# Revit family: КСФ К2 ЕС_Eng
name_source: partatom
category: Mechanical Equipment
units: mm (PartAtom-declared; Revit-internal decimal feet)

## family parameters
Always vertical = Yes
Classification = None
Cut with Voids When Loaded = No
Part Type = Normal
Room Calculation Point = No
Round Connector Dimension = Use Diameter
Shared = No
Work Plane-Based = No

## types (6) — shared parameters
00_20_Manufacturer = Vents
00_20_Name = Centrifugal duct fan
Casing Material = Steel, galvanized
Description = Heat- and sound-insulated casing
Frequency = 50 Hz
Load Classification = HVAC
Maintenance zone material = <By Category>
Manufacturer = Vents
Number of Fase = 1
Temperature of moving air = -25...+50 °C
URL = https://ventilation-system.com
Voltage = 230 V
a = 47 mm
w = 50 mm  [stored 0.164042 ft]
zero-valued in all types: Default Elevation

## per-type parameters (varying)
| type | Amperage | Apparent Load | B | B1 | B2 | D | Diameter | Dy | H | Height | L1 | L2 | Length | Maximum Air Flow | Power | Sound pressure level at 3 m distance | Weight | Width | b1 | h |
| KSF 100 К2 EC | 1 A | 212 VA | 512 mm  [stored 1.67979 ft] | 360 mm  [stored 1.1811 ft] | 589 mm | 97 mm  [stored 0.318241 ft] | 97 mm  [stored 0.318241 ft] | 92 mm  [stored 0.301837 ft] | 280 mm  [stored 0.918635 ft] | 280 mm  [stored 0.918635 ft] | 553 mm  [stored 1.8143 ft] | 460 mm  [stored 1.50919 ft] | 553 mm  [stored 1.8143 ft] | 353.0 m³/h | 118 W | 33 dBA | 17.00 kg | 512 mm  [stored 1.67979 ft] | 180 mm  [stored 0.590551 ft] | 69 mm |
| KSF 125 К2 EC | 1 A | 212 VA | 512 mm  [stored 1.67979 ft] | 360 mm  [stored 1.1811 ft] | 589 mm | 122 mm  [stored 0.400262 ft] | 122 mm  [stored 0.400262 ft] | 117 mm  [stored 0.383858 ft] | 280 mm  [stored 0.918635 ft] | 280 mm  [stored 0.918635 ft] | 553 mm  [stored 1.8143 ft] | 460 mm  [stored 1.50919 ft] | 553 mm  [stored 1.8143 ft] | 393.0 m³/h | 118 W | 33 dBA | 17.00 kg | 512 mm  [stored 1.67979 ft] | 180 mm  [stored 0.590551 ft] | 81 mm  [stored 0.265748 ft] |
| KSF 150 К2 EC | 1 A | 136 VA | 592 mm  [stored 1.94226 ft] | 390 mm  [stored 1.27953 ft] | 669 mm | 147 mm  [stored 0.482283 ft] | 147 mm  [stored 0.482283 ft] | 142 mm  [stored 0.465879 ft] | 350 mm  [stored 1.14829 ft] | 350 mm  [stored 1.14829 ft] | 613 mm | 520 mm  [stored 1.70604 ft] | 613 mm | 779.0 m³/h | 220 W | 38 dBA | 24.00 kg | 592 mm  [stored 1.94226 ft] | 195 mm  [stored 0.639764 ft] | 94 mm |
| KSF 160 К2 EC | 1 A | 136 VA | 592 mm  [stored 1.94226 ft] | 390 mm  [stored 1.27953 ft] | 669 mm | 157 mm  [stored 0.515092 ft] | 157 mm  [stored 0.515092 ft] | 152 mm | 350 mm  [stored 1.14829 ft] | 350 mm  [stored 1.14829 ft] | 613 mm | 520 mm  [stored 1.70604 ft] | 613 mm | 779.0 m³/h | 220 W | 38 dBA | 24.00 kg | 592 mm  [stored 1.94226 ft] | 195 mm  [stored 0.639764 ft] | 99 mm |
| KSF 200 К2 EC | 1 A | 334 VA | 552 mm  [stored 1.81102 ft] | 374 mm  [stored 1.22703 ft] | 629 mm | 197 mm | 197 mm | 192 mm  [stored 0.629921 ft] | 380 mm | 380 mm | 646 mm | 553 mm  [stored 1.8143 ft] | 646 mm | 1264.0 m³/h | 259 W | 40 dBA | 26.00 kg | 552 mm  [stored 1.81102 ft] | 187 mm  [stored 0.613517 ft] | 119 mm |
| KSF 250 К2 EC | 2 A | 407 VA | 665 mm | 487 mm  [stored 1.59777 ft] | 742 mm | 247 mm | 247 mm | 242 mm  [stored 0.793963 ft] | 411 mm  [stored 1.34843 ft] | 411 mm  [stored 1.34843 ft] | 699 mm | 606 mm | 699 mm | 1682.0 m³/h | 374 W | 41 dBA | 33.00 kg | 665 mm | 244 mm | 144 mm |

note: column(s) folded — value = type name in every type: 00_20_Type

note: [stored X ft] marks values corroborated as IEEE doubles in the binary element streams (Revit-internal decimal feet)
